# Revit family: Precast Stemmed Deck Members-Double Tee-Section
name_source: partatom
category: Detail Items
revit_build: Autodesk Revit Architecture 2012 (Build: 20110210_1515)
units: mm (PartAtom-declared; Revit-internal decimal feet)

## types (36) — shared parameters
Slab Depth = 0' - 2"

## per-type parameters (varying)
| type | Bottom Tee Width | Depth | Keynote | Space | Tdepth | Top Tee Width | Width |
| 8DT12 | 0' - 3 3/4" | 1' - 0" | 03 41 00.G1 | 4' - 0" | 0' - 0" | 0' - 5 3/4" | 8' - 0" |
| 8DT12+2 | 0' - 3 3/4" | 1' - 0" | 03 41 00.G2 | 4' - 0" | 0' - 2" | 0' - 5 3/4" | 8' - 0" |
| 8LDT12 | 0' - 3 3/4" | 1' - 0" | 03 41 00.G3 | 4' - 0" | 0' - 0" | 0' - 5 3/4" | 8' - 0" |
| 8LDT12+2 | 0' - 3 3/4" | 1' - 0" | 03 41 00.G4 | 4' - 0" | 0' - 2" | 0' - 5 3/4" | 8' - 0" |
| 8DT14 | 0' - 3 3/4" | 1' - 2" | 03 41 00.G5 | 4' - 0" | 0' - 0" | 0' - 5 3/4" | 8' - 0" |
| 8DT14+2 | 0' - 3 3/4" | 1' - 2" | 03 41 00.G6 | 4' - 0" | 0' - 2" | 0' - 5 3/4" | 8' - 0" |
| 8LDT14 | 0' - 3 3/4" | 1' - 2" | 03 41 00.G7 | 4' - 0" | 0' - 0" | 0' - 5 3/4" | 8' - 0" |
| 8LDT14+2 | 0' - 3 3/4" | 1' - 2" | 03 41 00.G8 | 4' - 0" | 0' - 2" | 0' - 5 3/4" | 8' - 0" |
| 8DT16 | 0' - 3 3/4" | 1' - 4" | 03 41 00.G9 | 4' - 0" | 0' - 0" | 0' - 5 3/4" | 8' - 0" |
| 8DT16+2 | 0' - 3 3/4" | 1' - 4" | 03 41 00.G10 | 4' - 0" | 0' - 2" | 0' - 5 3/4" | 8' - 0" |
| 8LDT16 | 0' - 3 3/4" | 1' - 4" | 03 41 00.G11 | 4' - 0" | 0' - 0" | 0' - 5 3/4" | 8' - 0" |
| 8LDT16+2 | 0' - 3 3/4" | 1' - 4" | 03 41 00.G12 | 4' - 0" | 0' - 2" | 0' - 5 3/4" | 8' - 0" |
| 8DT18 | 0' - 3 3/4" | 1' - 6" | 03 41 00.G13 | 4' - 0" | 0' - 0" | 0' - 5 3/4" | 8' - 0" |
| 8DT18+2 | 0' - 3 3/4" | 1' - 6" | 03 41 00.G14 | 4' - 0" | 0' - 2" | 0' - 5 3/4" | 8' - 0" |
| 8LDT18 | 0' - 3 3/4" | 1' - 6" | 03 41 00.G15 | 4' - 0" | 0' - 0" | 0' - 5 3/4" | 8' - 0" |
| 8LDT18+2 | 0' - 3 3/4" | 1' - 4" | 03 41 00.G16 | 4' - 0" | 0' - 2" | 0' - 5 3/4" | 8' - 0" |
| 8DT20 | 0' - 3 3/4" | 1' - 8" | 03 41 00.G17 | 4' - 0" | 0' - 0" | 0' - 5 3/4" | 8' - 0" |
| 8DT20+2 | 0' - 3 3/4" | 1' - 8" | 03 41 00.G18 | 4' - 0" | 0' - 2" | 0' - 5 3/4" | 8' - 0" |
| 8LDT20 | 0' - 3 3/4" | 1' - 8" | 03 41 00.G19 | 4' - 0" | 0' - 0" | 0' - 5 3/4" | 8' - 0" |
| 8LDT20+2 | 0' - 3 3/4" | 1' - 8" | 03 41 00.G20 | 4' - 0" | 0' - 2" | 0' - 5 3/4" | 8' - 0" |
| 8DT24 | 0' - 3 3/4" | 2' - 0" | 03 41 00.G21 | 4' - 0" | 0' - 0" | 0' - 5 3/4" | 8' - 0" |
| 8DT24+2 | 0' - 3 3/4" | 2' - 0" | 03 41 00.G22 | 4' - 0" | 0' - 2" | 0' - 5 3/4" | 8' - 0" |
| 8LDT24 | 0' - 3 3/4" | 2' - 0" | 03 41 00.G23 | 4' - 0" | 0' - 0" | 0' - 5 3/4" | 8' - 0" |
| 8LDT24+2 | 0' - 3 3/4" | 2' - 0" | 03 41 00.G24 | 4' - 0" | 0' - 2" | 0' - 5 3/4" | 8' - 0" |
| 8DT32 | 0' - 4 3/4" | 2' - 8" | 03 41 00.G25 | 4' - 0" | 0' - 0" | 0' - 7 3/4" | 8' - 0" |
| 8DT32+2 | 0' - 4 3/4" | 2' - 8" | 03 41 00.G26 | 4' - 0" | 0' - 2" | 0' - 7 3/4" | 8' - 0" |
| 8LDT32 | 0' - 4 3/4" | 2' - 8" | 03 41 00.G27 | 4' - 0" | 0' - 0" | 0' - 7 3/4" | 8' - 0" |
| 8LDT32+2 | 0' - 4 3/4" | 2' - 8" | 03 41 00.G28 | 4' - 0" | 0' - 2" | 0' - 7 3/4" | 8' - 0" |
| 10DT24 | 0' - 3 3/4" | 2' - 0" | 03 41 00.G29 | 6' - 0" | 0' - 0" | 0' - 5 3/4" | 10' - 0" |
| 10DT24+2 | 0' - 3 3/4" | 2' - 0" | 03 41 00.G30 | 6' - 0" | 0' - 2" | 0' - 5 3/4" | 10' - 0" |
| 10LDT24 | 0' - 3 3/4" | 2' - 0" | 03 41 00.G31 | 6' - 0" | 0' - 0" | 0' - 5 3/4" | 10' - 0" |
| 10LDT24+2 | 0' - 3 3/4" | 2' - 0" | 03 41 00.G32 | 6' - 0" | 0' - 2" | 0' - 5 3/4" | 10' - 0" |
| 10DT32 | 0' - 4 3/4" | 2' - 8" | 03 41 00.G33 | 6' - 0" | 0' - 0" | 0' - 7 3/4" | 10' - 0" |
| 10DT32+2 | 0' - 4 3/4" | 2' - 8" | 03 41 00.G34 | 6' - 0" | 0' - 2" | 0' - 7 3/4" | 10' - 0" |
| 10LDT32 | 0' - 4 3/4" | 2' - 8" | 03 41 00.G35 | 6' - 0" | 0' - 0" | 0' - 7 3/4" | 10' - 0" |
| 10LDT32+2 | 0' - 4 3/4" | 2' - 8" | 03 41 00.G36 | 6' - 0" | 0' - 2" | 0' - 7 3/4" | 10' - 0" |

## geometry (parser evidence)
native form markers: Sweep x1
no freeform markers — native parametric forms only
